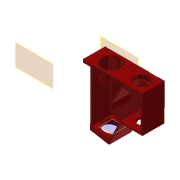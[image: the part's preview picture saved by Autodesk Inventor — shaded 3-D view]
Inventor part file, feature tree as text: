
AUTODESK INVENTOR PART (.ipt)
format: ipt  version: 2022 (Build 260153000, 153)  size: 390,144 bytes
history: native  units: mm
features: other x16, sketch x15, reference x15, extrude x13, plane x6, projected_geometry x6, hole x2, pattern_linear x1
ambient origin geometry x8: Origin, YZ Plane, XZ Plane, XY Plane, X Axis, Y Axis, Z Axis, Center Point
bodies: Solid1 (feature_tree)
feature tree (74):
  plane  "Work Plane1"
  plane  "Work Plane2"
  extrude  "Extrusion1"  TaperAngle=180.0deg  [1 undecoded]
  extrude  "Extrusion2"  Depth=3.0mm TaperAngle=0.0deg
  plane  "Work Plane3"
  plane  "Work Plane4"
  extrude  "Extrusion5"  Depth=3.0mm
  plane  "Work Plane5"
  extrude  "Extrusion9"  Depth=30.7mm
  plane  "Arbeitsebene11"
  extrude  "Extrusion17"  Depth=15.0mm TaperAngle=0.0deg
  extrude  "Extrusion18"  Depth=2.0mm
  hole  "Bohrung4"  [1 undecoded]
  pattern_linear  "Rechteckige Anordnung1"  Count1=6  [1 undecoded]
  extrude  "Extrusion21"  Depth=7.5mm
  extrude  "Extrusion23"  Depth=3.0mm
  hole  "Bohrung5"  [1 undecoded]
  extrude  "Extrusion24"  Depth=3.0mm
  extrude  "Extrusion25"  Depth=28.0mm
  extrude  "Extrusion26"  Depth=7.5mm TaperAngle=0.0deg
  extrude  "Extrusion27"  Depth=7.5mm
  extrude  "Extrusion28"  Depth=7.5mm
  sketch  "Sketch2"  dims[d0=4.0mm d1=180.0deg]
  sketch  "Sketch3"  dims[d2=3.0mm d6=4.0mm d7=0.0mm d8=3.0mm d14=32.0mm d15=0.0mm]
  sketch  "Sketch7"  dims[d23=3.0mm d33=24.0mm]
  sketch  "Sketch11"  dims[d34=5.0mm d35=0.0mm d43=30.7mm]
  sketch  "Sketch21"  dims[d44=60.0mm d45=0.0mm d101=15.0mm d102=0.0mm]
  sketch  "Sketch22"  dims[d104=2.0mm d105=0.0mm d110=8.0mm]
  projected_geometry  "Projected Loop10"
  sketch  "Skizze26"  dims[d124=2.8mm d125=6.0mm d126=4.0mm d127=2.0mm d128=90.0deg d129=12.0mm d130=20.594885mm d131=120.0mm d133=12.5mm]
  reference  "Referenz23"
  reference  "Referenz24"
  reference  "Referenz25"
  reference  "Referenz26"
  sketch  "Skizze28"  dims[d134=1.0mm]
  reference  "Referenz27"
  reference  "Referenz28"
  projected_geometry  "Projizierte Kontur12"
  reference  "Referenz32"
  reference  "Referenz33"
  reference  "Referenz34"
  reference  "Referenz35"
  reference  "Referenz36"
  sketch  "Skizze30"  dims[d135=1.0mm]
  sketch  "Skizze31"  dims[d136=0.5mm d137=0.0mm]
  projected_geometry  "Projizierte Kontur13"
  sketch  "Skizze32"  dims[d156=3.0mm]
  projected_geometry  "Projizierte Kontur14"
  sketch  "Skizze34"  dims[d157=3.0mm]
  projected_geometry  "Projizierte Kontur16"
  sketch  "Skizze35"  dims[d158=1.0mm]
  reference  "Referenz40"
  sketch  "Skizze36"  dims[d159=94.0mm]
  reference  "Referenz41"
  reference  "Referenz42"
  sketch  "Skizze37"  dims[d160=85.0mm d161=60.0mm d163=34.0mm d165=3.0mm d166=3.0mm d167=3.0mm d168=28.0mm d169=5.0mm d170=0.0mm d171=25.5mm d172=5.0mm d173=3.0mm d174=6.0mm d175=8.0mm d176=5.0mm d177=90.0deg d178=8.0mm d179=20.594885mm d180=12.0mm d181=5.0mm d182=2.8mm d183=2.8mm d185=2.8mm d186=2.8mm d187=12.0mm d188=12.0mm d189=0.0mm d190=42.0mm d191=0.0mm d192=0.0mm d193=20.0mm d194=0.0mm d202=10.0mm d203=0.0mm d204=25.4mm d205=20.0mm d206=1.0mm d207=0.0mm d208=25.4mm d209=1.0mm d210=0.0mm d211=10.0mm d213=1.0mm d214=15.0mm d215=29.5mm d216=7.5mm d217=15.0mm d218=0.0mm]
  projected_geometry  "Projizierte Kontur17"
  reference  "Referenz43"
  other  "<userpath>\Downloads\cellSTORM\cellSTORM_v5_microsocpe.iam"
  other  "cellSTORM_v5_microsocpe.iam"
  other  "30_Cube_Z_Focus_MGN_NEMA_rail:1"
  other  "00_MGN12H, LINEAR GUIDE BLOCK:1"
  other  "<userpath>\Documents\GitHub\cellstorm\INVENTOR\cellSTORM_v5_microsocpe.iam"
  other  "PF10-03-P01-Step:3"
  other  "30_Cube_Z_Focus_MGN12_NEMA_slide_part2:1"
  other  "PF10-03-P01-Step:4"
  other  "00_Eyepiece_20x_WF:1"
  other  "cellSTORM_lightpath:2"
  other  "<userpath>\Documents\GitHub\cellstorm\INVENTOR\cellSTORM_v6.iam"
  other  "cellSTORM_v6.iam"
  other  "00_Arduino_CNC_Assembly:1"
  other  "Arduino_Uno_CNC_Shield_V3_2"
  other  "cellSTORM_v5.iam"
  other  "cellSTORM_v5_cellphonestage:1"
note: 4 required parameter values undecoded (feature->parameter linkage not recoverable at this tier; creation-order binding heuristic only, values carry confidence <= 0.55)
